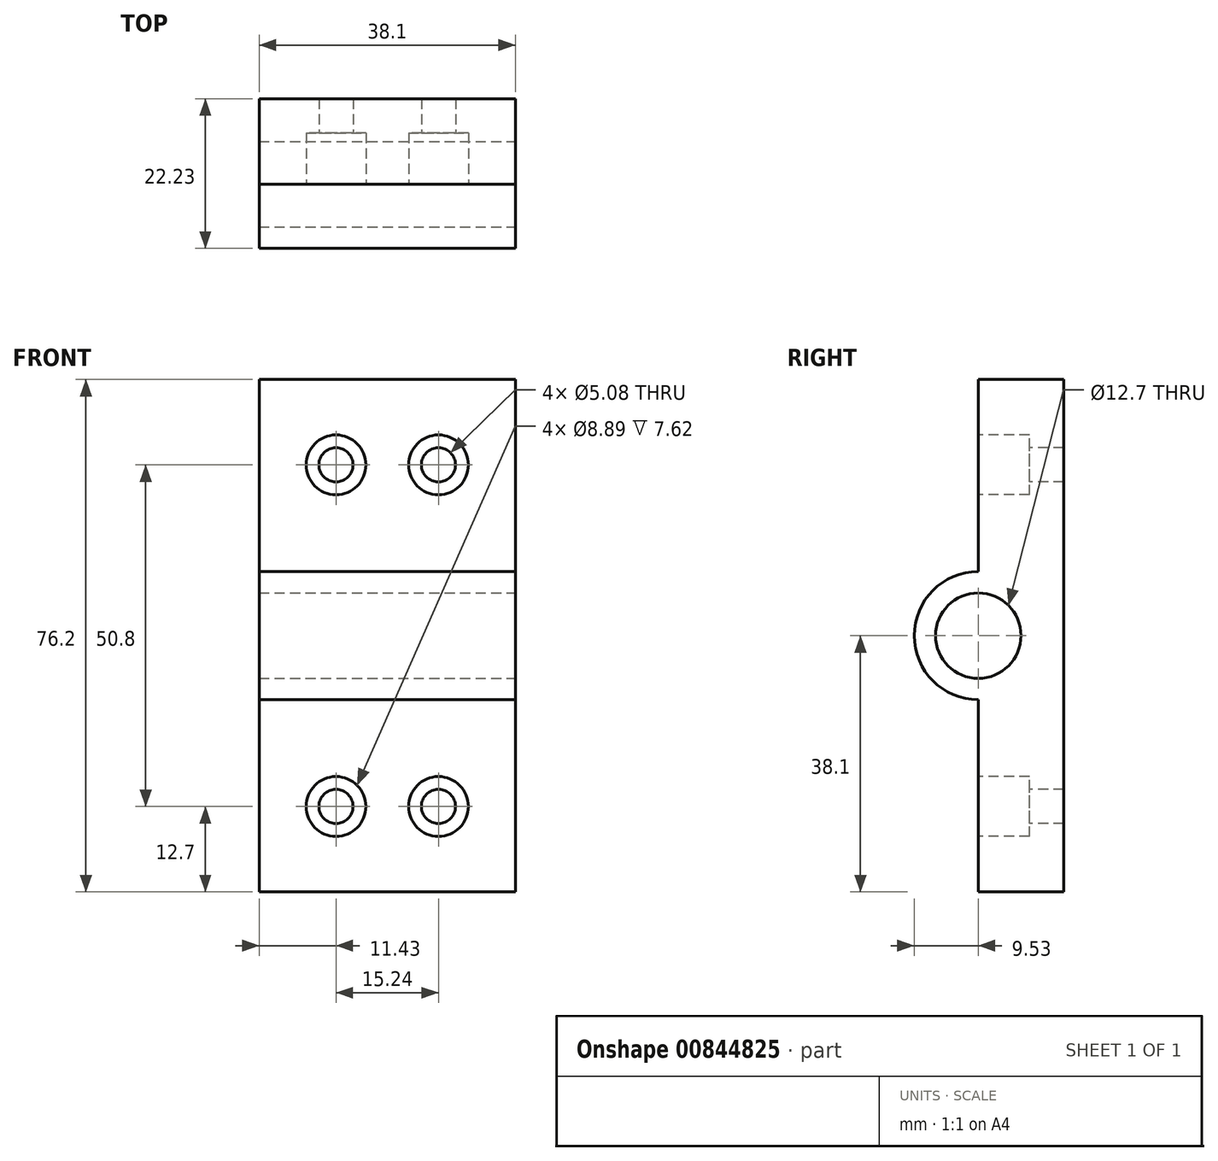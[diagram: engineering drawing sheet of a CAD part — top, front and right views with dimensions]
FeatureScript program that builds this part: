
annotation { "Feature Type Name" : "Feature", "Feature Type Description" : "" }
export const myFeature = defineFeature(function(context is Context, id is Id, definition is map)
    precondition{}
    {
        {
            var Q0;
            Q0=qCreatedBy(makeId("Front.planeOp"),FACE);
            var sketch = newSketch(context, id + "F0", { "sketchPlane" : qUnion([Q0])});
            skLineSegment(sketch, "E0.bottom", {"start": v(19.05, -38.1) * mm, "end": v(-19.05, -38.1) * mm});
            skLineSegment(sketch, "E0.top", {"start": v(19.05, 38.1) * mm, "end": v(-19.05, 38.1) * mm});
            skLineSegment(sketch, "E0.left", {"start": v(19.05, -38.1) * mm, "end": v(19.05, 38.1) * mm});
            skLineSegment(sketch, "E0.right", {"start": v(-19.05, -38.1) * mm, "end": v(-19.05, 38.1) * mm});
            skPoint(sketch, "E0.middle", {"position": v(0, 0) * mm});
            skSolve(sketch);
        }
        {
            var Q0;
            Q0 = qSketchRegion(id + "F0", true);
            extrude(context, id + "F1", {"entities" : qUnion([Q0]), "depth" : 12.7 * mm, "offsetDistance" : 25.4 * mm});
        }
        {
            var Q0;
            Q0=makeQuery(id+"F1.opExtrude","SWEPT_FACE",FACE,{"disambiguationData":[OSD([sQuery(id+"F0.wireOp",EDGE,"E0.left")])]});
            var sketch = newSketch(context, id + "F2", { "sketchPlane" : qUnion([Q0])});
            skCircle(sketch, "E1", {"center": v(-12.7, 0) * mm, "radius": 9.53 * mm});
            skSolve(sketch);
        }
        {
            var Q0;
            Q0 = qSketchRegion(id + "F2", true);
            extrude(context, id + "F3", {"entities" : qUnion([Q0]), "operationType" : NewBodyOperationType.ADD, "oppositeDirection" : true, "depth" : 38.1 * mm, "offsetDistance" : 25.4 * mm});
        }
        {
            var Q0;
            Q0=makeQuery(id+"F3.boolean.opBoolean","MERGE",FACE,{"derivedFrom":[makeQuery(id+"F1.opExtrude","SWEPT_FACE",FACE,{"disambiguationData":[OSD([sQuery(id+"F0.wireOp",EDGE,"E0.left")])]}),makeQuery(id+"F3.opExtrude","CAP_FACE",FACE,{"disambiguationData":[OSD([sQuery(id+"F2.wireOp",EDGE,"E1")])],"isStart":true})]});
            var sketch = newSketch(context, id + "F4", { "sketchPlane" : qUnion([Q0])});
            skCircle(sketch, "E2", {"center": v(-12.7, 0) * mm, "radius": 6.35 * mm});
            skSolve(sketch);
        }
        {
            var Q0;
            Q0 = qSketchRegion(id + "F4", true);
            extrude(context, id + "F5", {"entities" : qUnion([Q0]), "operationType" : NewBodyOperationType.REMOVE, "oppositeDirection" : true, "depth" : 40.4 * mm, "offsetDistance" : 25.4 * mm});
        }
        {
            var Q0;
            {var subQ0=sQuery(id+"F0.wireOp",EDGE,"E0.right");var subQ1=sQuery(id+"F0.wireOp",EDGE,"E0.left");var subQ3=sQuery(id+"F0.wireOp",EDGE,"E0.top");Q0=makeQuery(id+"F3.boolean.opBoolean","SPLIT",FACE,{"disambiguationData":[TD([makeQuery(id+"F1.opExtrude","SWEPT_FACE",FACE,{"disambiguationData":[OSD([subQ3])]})])],"derivedFrom":makeQuery(id+"F1.opExtrude","CAP_FACE",FACE,{"disambiguationData":[OSD([sQuery(id+"F0.wireOp",EDGE,"E0.bottom"),subQ3,subQ1,subQ0])],"isStart":false})});}
            var sketch = newSketch(context, id + "F6", { "sketchPlane" : qUnion([Q0])});
            skCircle(sketch, "E3", {"center": v(-7.62, 25.4) * mm, "radius": 2.54 * mm});
            skCircle(sketch, "E4.MirrorC", {"center": v(7.62, 25.4) * mm, "radius": 2.54 * mm});
            skCircle(sketch, "E5.MirrorC", {"center": v(-7.62, -25.4) * mm, "radius": 2.54 * mm});
            skCircle(sketch, "E6.MirrorC", {"center": v(7.62, -25.4) * mm, "radius": 2.54 * mm});
            skSolve(sketch);
        }
        {
            var Q0;
            Q0 = qSketchRegion(id + "F6", true);
            extrude(context, id + "F7", {"entities" : qUnion([Q0]), "operationType" : NewBodyOperationType.REMOVE, "oppositeDirection" : true, "depth" : 25.4 * mm, "offsetDistance" : 25.4 * mm});
        }
        {
            var Q0;
            {var subQ0=sQuery(id+"F0.wireOp",EDGE,"E0.right");var subQ1=sQuery(id+"F0.wireOp",EDGE,"E0.left");var subQ3=sQuery(id+"F0.wireOp",EDGE,"E0.top");Q0=makeQuery(id+"F3.boolean.opBoolean","SPLIT",FACE,{"disambiguationData":[TD([makeQuery(id+"F1.opExtrude","SWEPT_FACE",FACE,{"disambiguationData":[OSD([subQ3])]})])],"derivedFrom":makeQuery(id+"F1.opExtrude","CAP_FACE",FACE,{"disambiguationData":[OSD([sQuery(id+"F0.wireOp",EDGE,"E0.bottom"),subQ3,subQ1,subQ0])],"isStart":false})});}
            var sketch = newSketch(context, id + "F8", { "sketchPlane" : qUnion([Q0])});
            skCircle(sketch, "E7", {"center": v(-7.62, 25.4) * mm, "radius": 4.45 * mm});
            skCircle(sketch, "E8", {"center": v(7.62, 25.4) * mm, "radius": 4.45 * mm});
            skCircle(sketch, "E9", {"center": v(-7.62, -25.4) * mm, "radius": 4.45 * mm});
            skCircle(sketch, "E10", {"center": v(7.62, -25.4) * mm, "radius": 4.45 * mm});
            skSolve(sketch);
        }
        {
            var Q0;
            Q0 = qSketchRegion(id + "F8", true);
            extrude(context, id + "F9", {"entities" : qUnion([Q0]), "operationType" : NewBodyOperationType.REMOVE, "oppositeDirection" : true, "depth" : 7.62 * mm, "offsetDistance" : 25.4 * mm});
        }
    });
